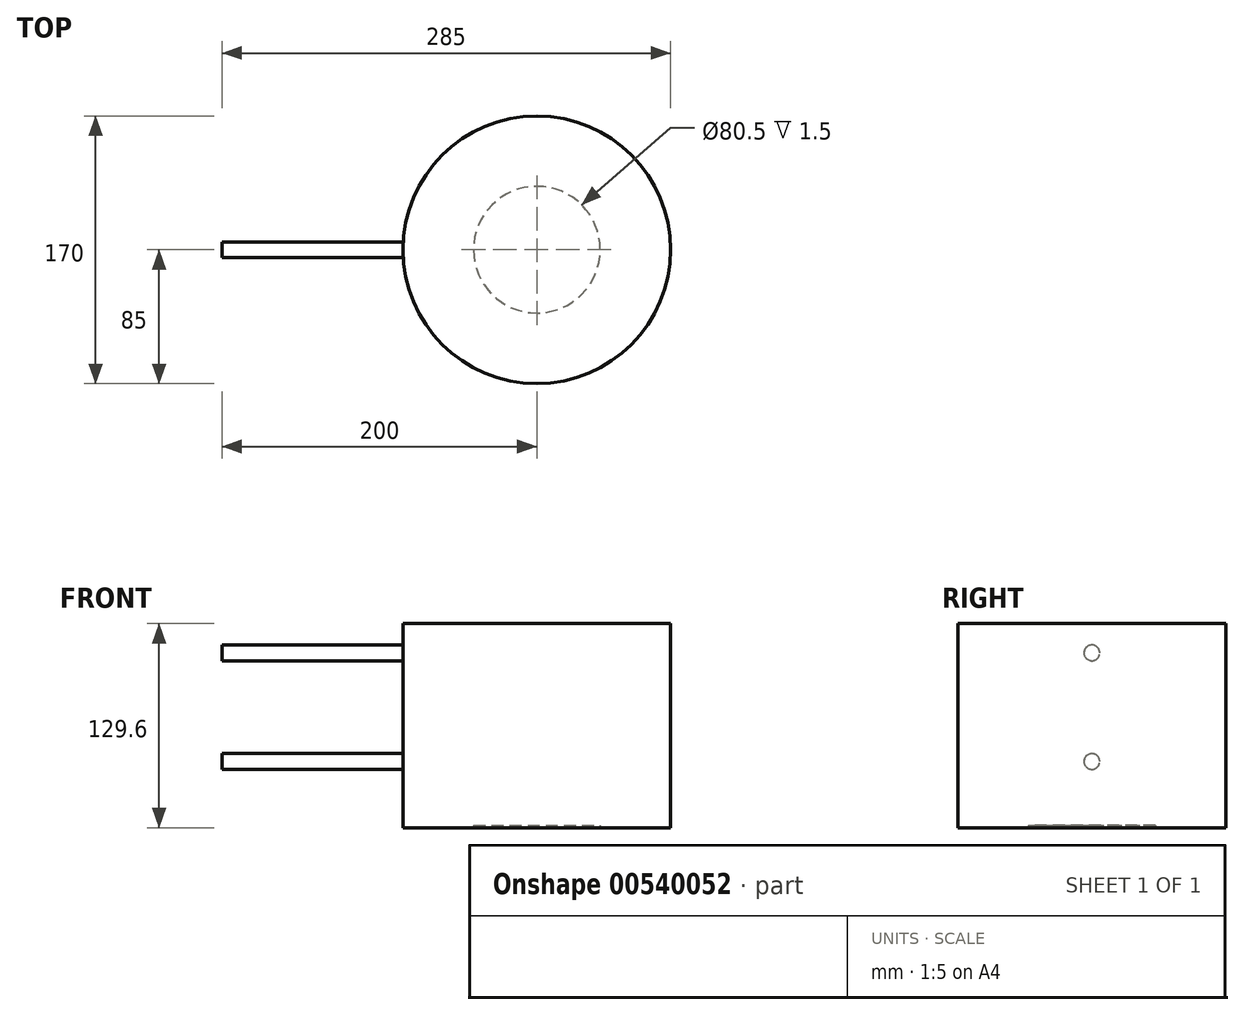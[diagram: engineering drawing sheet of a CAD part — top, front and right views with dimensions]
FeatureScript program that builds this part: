
annotation { "Feature Type Name" : "Feature", "Feature Type Description" : "" }
export const myFeature = defineFeature(function(context is Context, id is Id, definition is map)
    precondition{}
    {
        {
            var Q0;
            Q0=qCreatedBy(makeId("Top.planeOp"),FACE);
            var sketch = newSketch(context, id + "F0", { "sketchPlane" : qUnion([Q0])});
            skCircle(sketch, "E0", {"center": v(0, 0) * mm, "radius": 85 * mm});
            skSolve(sketch);
        }
        {
            var Q0;
            Q0=makeQuery(id+"F0.imprint","IMPRINT",FACE,{"disambiguationData":[TD([[makeQuery(id+"F0.imprint","IMPRINT",EDGE,{"derivedFrom":sQuery(id+"F0.wireOp",EDGE,"E0")}),1.0]])]});
            extrude(context, id + "F1", {"entities" : qUnion([Q0]), "depth" : 129.6 * mm, "offsetDistance" : 25 * mm});
        }
        {
            var Q0;
            Q0=qCreatedBy(makeId("Right.planeOp"),FACE);
            var sketch = newSketch(context, id + "F2", { "sketchPlane" : qUnion([Q0])});
            skCircle(sketch, "E1", {"center": v(0, 42) * mm, "radius": 5 * mm});
            skCircle(sketch, "E2", {"center": v(0, 111) * mm, "radius": 5 * mm});
            skSolve(sketch);
        }
        {
            var Q0;
            Q0 = qSketchRegion(id + "F2", true);
            extrude(context, id + "F3", {"entities" : qUnion([Q0]), "operationType" : NewBodyOperationType.ADD, "oppositeDirection" : true, "depth" : 200 * mm, "offsetDistance" : 25 * mm});
        }
        {
            var Q0;
            Q0=makeQuery(id+"F1.opExtrude","CAP_FACE",FACE,{"disambiguationData":[OSD([sQuery(id+"F0.wireOp",EDGE,"E0")])],"isStart":true});
            var sketch = newSketch(context, id + "F4", { "sketchPlane" : qUnion([Q0])});
            skCircle(sketch, "E3", {"center": v(0, 0) * mm, "radius": 40.25 * mm});
            skSolve(sketch);
        }
        {
            var Q0;
            Q0=makeQuery(id+"F4.imprint","IMPRINT",FACE,{"disambiguationData":[TD([[makeQuery(id+"F4.imprint","IMPRINT",EDGE,{"derivedFrom":sQuery(id+"F4.wireOp",EDGE,"E3")}),1.0]])]});
            extrude(context, id + "F5", {"entities" : qUnion([Q0]), "operationType" : NewBodyOperationType.REMOVE, "oppositeDirection" : true, "depth" : 1.5 * mm, "offsetDistance" : 25 * mm});
        }
    });
